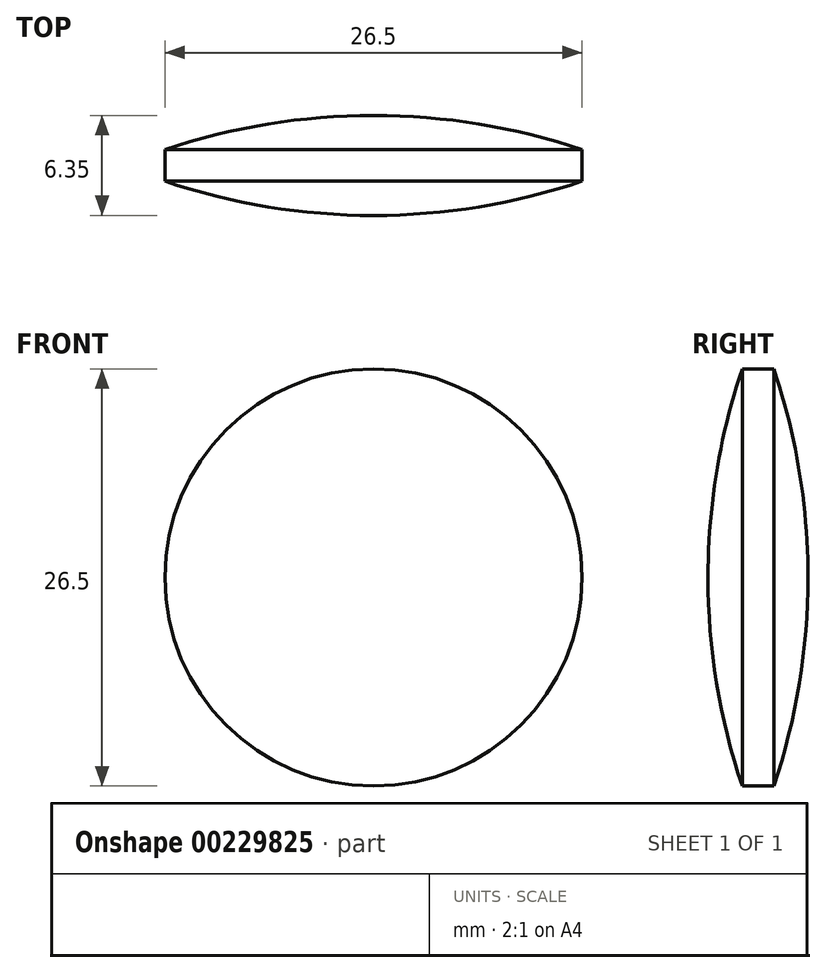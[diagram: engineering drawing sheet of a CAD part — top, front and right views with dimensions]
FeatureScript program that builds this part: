
annotation { "Feature Type Name" : "Feature", "Feature Type Description" : "" }
export const myFeature = defineFeature(function(context is Context, id is Id, definition is map)
    precondition{}
    {
        {
            var Q0;
            Q0=qCreatedBy(makeId("Right.planeOp"),FACE);
            var sketch = newSketch(context, id + "F0", { "sketchPlane" : qUnion([Q0])});
            skLineSegment(sketch, "E0", {"start": v(-1, 13.25) * mm, "end": v(1, 13.25) * mm});
            skLineSegment(sketch, "E1", {"start": v(0, 0) * mm, "end": v(0, 13.25) * mm, "construction": true});
            skLineSegment(sketch, "E2", {"start": v(-3.18, 0) * mm, "end": v(3.18, 0) * mm});
            skLineSegment(sketch, "E3.MirrorCS", {"start": v(0, 0) * mm, "end": v(0, -13.25) * mm, "construction": true});
            skLineSegment(sketch, "E4.MirrorCS", {"start": v(-1, -13.25) * mm, "end": v(1, -13.25) * mm, "construction": true});
            skArc(sketch, "E5", {"start": v(-1, 13.25) * mm, "mid": v(-2.63, 6.71) * mm, "end": v(-3.18, 0) * mm});
            skArc(sketch, "E6", {"start": v(3.17, 0) * mm, "mid": v(2.63, 6.71) * mm, "end": v(1, 13.25) * mm});
            skSolve(sketch);
        }
        {
            var Q0;
            Q0 = qSketchRegion(id + "F0", true);
            var Q1;
            Q1=sQuery(id+"F0.wireOp",EDGE,"E2");
            revolve(context, id + "F1", {"entities" : qUnion([Q0]), "axis" : qUnion([Q1]), "revolveType" : RevolveType.FULL});
        }
    });
